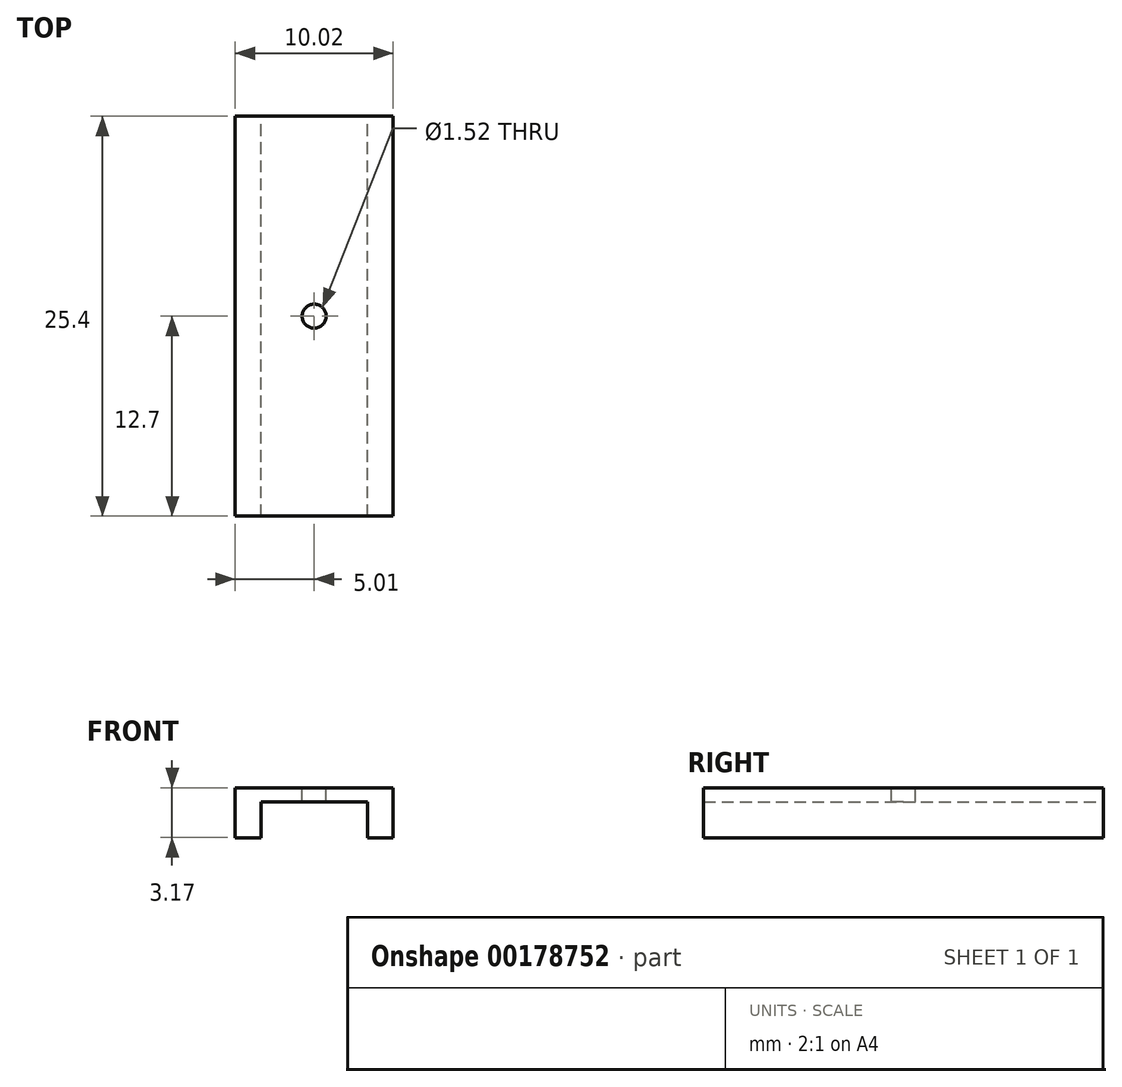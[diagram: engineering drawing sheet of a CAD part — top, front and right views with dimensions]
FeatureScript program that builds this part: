
annotation { "Feature Type Name" : "Feature", "Feature Type Description" : "" }
export const myFeature = defineFeature(function(context is Context, id is Id, definition is map)
    precondition{}
    {
        {
            var Q0;
            Q0=qCreatedBy(makeId("Front.planeOp"),FACE);
            var sketch = newSketch(context, id + "F0", { "sketchPlane" : qUnion([Q0])});
            skPoint(sketch, "E0.middle", {"position": v(0, 0) * mm});
            skLineSegment(sketch, "E1.top", {"start": v(5, 2.03) * mm, "end": v(-5, 2.03) * mm});
            skLineSegment(sketch, "E1.left", {"start": v(5, -1.14) * mm, "end": v(5, 2.03) * mm});
            skLineSegment(sketch, "E1.right", {"start": v(-5, -1.14) * mm, "end": v(-5, 2.03) * mm});
            skLineSegment(sketch, "E2.top", {"start": v(3.38, 1.14) * mm, "end": v(-3.38, 1.14) * mm});
            skLineSegment(sketch, "E2.left", {"start": v(3.38, -1.14) * mm, "end": v(3.38, 1.14) * mm});
            skLineSegment(sketch, "E2.right", {"start": v(-3.38, -1.14) * mm, "end": v(-3.38, 1.14) * mm});
            skLineSegment(sketch, "E3", {"start": v(-3.38, -1.14) * mm, "end": v(-5, -1.14) * mm});
            skPoint(sketch, "E3.endSnap0", {"position": v(-5, 0) * mm});
            skLineSegment(sketch, "E4", {"start": v(3.38, -1.14) * mm, "end": v(5, -1.14) * mm});
            skPoint(sketch, "E5.orphan", {"position": v(-5, -2.03) * mm});
            skPoint(sketch, "E6.orphan", {"position": v(5, -2.03) * mm});
            skSolve(sketch);
        }
        {
            var Q0;
            Q0 = qSketchRegion(id + "F0", true);
            extrude(context, id + "F1", {"entities" : qUnion([Q0]), "depth" : 25.4 * mm});
        }
        {
            var Q0;
            Q0=makeQuery(id+"F1.opExtrude","SWEPT_FACE",FACE,{"disambiguationData":[OSD([sQuery(id+"F0.wireOp",EDGE,"E1.top")])]});
            var sketch = newSketch(context, id + "F2", { "sketchPlane" : qUnion([Q0])});
            skCircle(sketch, "E7", {"center": v(0, -12.7) * mm, "radius": 0.76 * mm});
            skPoint(sketch, "E8.trimOffspring.end.orphan", {"position": v(0, -25.4) * mm});
            skPoint(sketch, "E9.start.orphan", {"position": v(0, 0) * mm});
            skSolve(sketch);
        }
        {
            var Q0;
            Q0 = qSketchRegion(id + "F2", true);
            extrude(context, id + "F3", {"entities" : qUnion([Q0]), "operationType" : NewBodyOperationType.REMOVE, "endBound" : BoundingType.THROUGH_ALL, "oppositeDirection" : true, "depth" : 25.4 * mm});
        }
    });
